FCSTD DOCUMENT  (FreeCAD 0.21R33771 (Git))
Label: YawBearing_Assembly
License: All rights reserved
LicenseURL: http://en.wikipedia.org/wiki/All_rights_reserved
objects: App::Link×4, App::Part×2, Spreadsheet::Sheet×1
EXTERNAL_REF file=YawBearing_Pipe.FCStd obj=Tube
EXTERNAL_REF file=YawBearing_Plate_Top.FCStd obj=PocketBody
EXTERNAL_REF file=../Master_of_Puppets.FCStd obj=Alternator
EXTERNAL_REF file=../Master_of_Puppets.FCStd obj=HighEndStop
EXTERNAL_REF file=../Master_of_Puppets.FCStd obj=Spreadsheet
EXTERNAL_REF file=../Master_of_Puppets.FCStd obj=YawBearing
EXTERNAL_REF file=YawBearing_ArcWireSupport.FCStd obj=PadBody
EXTERNAL_REF file=YawBearing_SafetyCatch.FCStd obj=Body

FEATURE [App::Link] Link  label="Pipe"
  LinkTransform = true
  LinkedObject = -> <external YawBearing_Pipe.FCStd>#Tube
FEATURE [App::Link] Link001  label="Plate_Top"
  LinkPlacement = pos=(-3.525,0,5.995) rot=(1,0,0;-1.5708rad)
  LinkedObject = -> <external YawBearing_Plate_Top.FCStd>#PocketBody
  Placement = pos=(-3.525,0,5.995) rot=(1,0,0;-1.5708rad)
  expr: .Placement.Base.x = Spreadsheet.TopPlateX
  expr: .Placement.Base.z = Spreadsheet.TopPlateZ
FEATURE [Spreadsheet::Sheet] Spreadsheet
  cells = A1='Inputs; A2='YawPipeDiameter; B2(YawPipeDiameter)==Master_of_Puppets#Spreadsheet.YawPipeDiameter; A3='FlatMetalThickness; B3(FlatMetalThickness)==Master_of_Puppets#Spreadsheet.FlatMetalThickness; A4='I; B4(I)==Master_of_Puppets#Alternator.I; A5='k; B5(k)==Master_of_Puppets#Alternator.k; A6='YawBearingPlateTopHoleRadius; B6(YawBearingPlateTopHoleRadius)==Master_of_Puppets#YawBearing.YawBearingPlateTopHoleRadius; A7='SafetyCatchZ; B7(SafetyCatchZ)==Master_of_Puppets#HighEndStop.SafetyCatchZ; A8='SafetyCatchPartAngle; B8(SafetyCatchPartAngle)==Master_of_Puppets#HighEndStop.SafetyCatchAngle; A9='YawPipeLength; B9(YawPipeLength)==Master_of_Puppets#HighEndStop.YawPipeLength; A10='ArcWireSupportLength; B10(ArcWireSupportLength)==Master_of_Puppets#YawBearing.ArcWireSupportLength; A11='Calculated; A12='TopPlateX; B12(TopPlateX)==-I / 2; A13='TopPlateZ; B13(TopPlateZ)==k / 2; A14='ArcWireSupportX; B14(ArcWireSupportX)==-ArcWireSupportLength / 2 - YawBearingPlateTopHoleRadius; A15='ArcWireSupportY; B15(ArcWireSupportY)==FlatMetalThickness; A16='SafetyCatchLinkY; B16(SafetyCatchLinkY)==(YawPipeLength - SafetyCatchZ) * -1; A17='SafetyCatchRotation; B17(SafetyCatchRotation)==create(<<rotation>>; 0; -90; 90); A18='SafetyCatchAxis; B18(SafetyCatchAxis)==.SafetyCatchRotation.Axis; A19='SafetyCatchAngle; B19(SafetyCatchAngle)==.SafetyCatchRotation.Angle * 180 / pi
FEATURE [App::Link] Link002  label="ArcWireSupport"
  LinkPlacement = pos=(-20.6,5,0) rot=(0,0,1;0rad)
  LinkedObject = -> <external YawBearing_ArcWireSupport.FCStd>#PadBody
  Placement = pos=(-20.6,5,0) rot=(0,0,1;0rad)
  expr: .Placement.Base.x = -Spreadsheet.ArcWireSupportLength / 2 - Spreadsheet.YawBearingPlateTopHoleRadius
  expr: .Placement.Base.y = Spreadsheet.ArcWireSupportY
FEATURE [App::Link] Link003  label="SafetyCatch"
  LinkPlacement = pos=(0,-22.4398,0) rot=(0.57735,-0.57735,0.57735;2.0944rad)
  LinkedObject = -> <external YawBearing_SafetyCatch.FCStd>#Body
  Placement = pos=(0,-22.4398,0) rot=(0.57735,-0.57735,0.57735;2.0944rad)
  expr: .LinkPlacement.Base.y = Spreadsheet.SafetyCatchLinkY
  expr: .Placement.Rotation.Angle = Spreadsheet.SafetyCatchAngle
  expr: .Placement.Rotation.Axis = Spreadsheet.SafetyCatchAxis
FEATURE [App::Part] Part001  label="SafetyCatchPart"
  Group = -> [Link003]
  Origin = -> Origin001
  Placement = pos=(0,0,0) rot=(0,-1,0;0.066334rad)
  expr: .Placement.Rotation.Angle = Spreadsheet.SafetyCatchPartAngle
FEATURE [App::Part] Part  label="YawBearing_Assembly"
  Group = -> [Link,Link001,Link002,Part001]
  Origin = -> Origin

RESOLVED EXTERNAL PARTS (link-assembly join: the EXTERNAL_REF files above that resolve inside this repo's crawl, each included once):
---- part ../Master_of_Puppets.FCStd = doc fcstd_6404554055c4 (61625 chars; too large to inline — full recipe in that document) ----
---- part YawBearing_ArcWireSupport.FCStd = doc fcstd_3435764e4c97 ----
FCSTD DOCUMENT  (FreeCAD 0.20R29177 (Git))
Label: YawBearing_ArcWireSupport
License: All rights reserved
LicenseURL: http://en.wikipedia.org/wiki/All_rights_reserved
objects: Sketcher::SketchObject×1, PartDesign::Pad×1, PartDesign::Body×1, Spreadsheet::Sheet×1
note: 4 computed .brp shape members not serialized (recipe doc carries the construction recipe); baked Part::Feature solids carry a one-line shape summary decoded from their .brp
EXTERNAL_REF file=../Master_of_Puppets.FCStd obj=YawBearing

FEATURE [Sketcher::SketchObject] Sketch
  FullyConstrained = true
  MapMode = 5
  Support = -> [XY_Plane001]
  expr: Constraints[8] = Spreadsheet.ArcWireSupportThickness
  expr: Constraints[9] = Spreadsheet.ArcWireSupportLength / 2
  sketch-geometry (4):
    g0: ArcOfCircle CenterX=0 CenterY=0 CenterZ=0 NormalX=0 NormalY=0 NormalZ=1 AngleXU=0 Radius=17.075 StartAngle=-9e-16 EndAngle=3.14159
    g1: ArcOfCircle CenterX=-1e-16 CenterY=0 CenterZ=0 NormalX=0 NormalY=0 NormalZ=1 AngleXU=0 Radius=22.075 StartAngle=-8.9e-15 EndAngle=3.14159
    g2: LineSegment StartX=-22.075 StartY=6.9728e-12 StartZ=0 EndX=-17.075 EndY=-1.268e-13 EndZ=0
    g3: LineSegment StartX=17.075 StartY=-1.52e-14 StartZ=0 EndX=22.075 EndY=-1.961e-13 EndZ=0
  constraints (12):
    c: Coincident(g0,g-1)
    c: PointOnObject(g0,g-1)
    c: PointOnObject(g0,g-1)
    c: Coincident(g1,g-1)
    c: PointOnObject(g1,g-1)
    c: Coincident(g2,g1)
    c: Coincident(g2,g0)
    c: Coincident(g3,g1)
    c: DistanceX(g2,g2) = 5
    c: DistanceX(g-2,g1) = 22.075
    c: Coincident(g0,g3)
    c: PointOnObject(g1,g-1)
FEATURE [PartDesign::Pad] Pad
  AllowMultiFace = false
  Direction = (0,0,1)
  Length = 10
  Length2 = 100
  Midplane = true
  Profile = -> Sketch
  Type = 0
  expr: Length = Spreadsheet.ArcWireSupportWidth
FEATURE [PartDesign::Body] PadBody  label="ArcWireSupport"
  Group = -> [Sketch,Pad]
  Origin = -> Origin001
  Tip = -> Pad
FEATURE [Spreadsheet::Sheet] Spreadsheet
  cells = A1=Inputs; A2=ArcWireSupportThickness; B2(ArcWireSupportThickness)==Master_of_Puppets#YawBearing.ArcWireSupportThickness; A3=ArcWireSupportWidth; B3(ArcWireSupportWidth)==Master_of_Puppets#YawBearing.ArcWireSupportWidth; A4=ArcWireSupportLength; B4(ArcWireSupportLength)==Master_of_Puppets#YawBearing.ArcWireSupportLength
---- part YawBearing_Plate_Top.FCStd = doc fcstd_9ede75f66de1 ----
FCSTD DOCUMENT  (FreeCAD 0.20R29177 (Git))
Label: YawBearing_Plate_Top
License: All rights reserved
LicenseURL: http://en.wikipedia.org/wiki/All_rights_reserved
objects: Sketcher::SketchObject×2, PartDesign::Pad×1, PartDesign::Pocket×1, PartDesign::Body×1, Spreadsheet::Sheet×1
note: 7 computed .brp shape members not serialized (recipe doc carries the construction recipe); baked Part::Feature solids carry a one-line shape summary decoded from their .brp
EXTERNAL_REF file=../Master_of_Puppets.FCStd obj=Alternator
EXTERNAL_REF file=../Master_of_Puppets.FCStd obj=Spreadsheet
EXTERNAL_REF file=../Master_of_Puppets.FCStd obj=YawBearing

FEATURE [Sketcher::SketchObject] Sketch
  FullyConstrained = true
  MapMode = 5
  Support = -> [XY_Plane001]
  expr: Constraints[14] = Spreadsheet.Width
  expr: Constraints[15] = Spreadsheet.Length
  sketch-geometry (6):
    g0: LineSegment StartX=-42.15 StartY=-42.65 StartZ=0 EndX=42.15 EndY=-42.65 EndZ=0
    g1: LineSegment StartX=42.15 StartY=-42.65 StartZ=0 EndX=42.15 EndY=42.65 EndZ=0
    g2: LineSegment StartX=42.15 StartY=42.65 StartZ=0 EndX=-42.15 EndY=42.65 EndZ=0
    g3: LineSegment StartX=-42.15 StartY=42.65 StartZ=0 EndX=-42.15 EndY=-42.65 EndZ=0
    g4: LineSegment StartX=-42.15 StartY=42.65 StartZ=0 EndX=42.15 EndY=-42.65 EndZ=0
    g5: LineSegment StartX=42.15 StartY=42.65 StartZ=0 EndX=-42.15 EndY=-42.65 EndZ=0
  constraints (16):
    c: Coincident(g0,g1)
    c: Coincident(g1,g2)
    c: Coincident(g2,g3)
    c: Coincident(g3,g0)
    c: Horizontal(g0)
    c: Horizontal(g2)
    c: Vertical(g1)
    c: Vertical(g3)
    c: Coincident(g4,g2)
    c: Coincident(g4,g0)
    c: Coincident(g5,g1)
    c: Coincident(g5,g0)
    c: PointOnObject(g-1,g4)
    c: PointOnObject(g-1,g5)
    c: DistanceX(g0,g0) = 84.3
    c: DistanceY(g1,g1) = 85.3
FEATURE [PartDesign::Pad] Pad
  AllowMultiFace = false
  Direction = (0,0,1)
  Length = 10
  Length2 = 100
  Profile = -> Sketch
  Type = 0
  expr: Length = Spreadsheet.FlatMetalThickness
FEATURE [Sketcher::SketchObject] Sketch001
  ExternalGeometry = -> [Pad]
  FullyConstrained = true
  MapMode = 5
  Placement = pos=(0,0,10) rot=(0,0,1;0rad)
  Support = -> [Pad]
  expr: Constraints[12] = Spreadsheet.Hole_x
  expr: Constraints[13] = Spreadsheet.Hole_y
  expr: Constraints[15] = Spreadsheet.YawBearingPlateTopHoleRadius
  expr: Constraints[17] = Spreadsheet.YawPipeRadius
  expr: Constraints[18] = Spreadsheet.YawPipeRadius
  expr: Constraints[19] = Spreadsheet.YawPipeRadius
  expr: Constraints[23] = Spreadsheet.Width
  expr: Constraints[25] = Spreadsheet.YawBearingPlateCornerChamferLength
  sketch-geometry (9):
    g0: LineSegment StartX=-42.15 StartY=-32.65 StartZ=0 EndX=-42.15 EndY=-42.65 EndZ=0
    g1: LineSegment StartX=-42.15 StartY=-42.65 StartZ=0 EndX=-32.15 EndY=-42.65 EndZ=0
    g2: LineSegment StartX=-32.15 StartY=-42.65 StartZ=0 EndX=-42.15 EndY=-32.65 EndZ=0
    g3: LineSegment StartX=-42.15 StartY=12.5 StartZ=0 EndX=12 EndY=12.5 EndZ=0
    g4: LineSegment StartX=12 StartY=12.5 StartZ=0 EndX=12 EndY=-42.65 EndZ=0
    g5: Circle CenterX=12 CenterY=12.5 CenterZ=0 NormalX=0 NormalY=0 NormalZ=1 AngleXU=0 Radius=10
    g6: ArcOfCircle CenterX=12 CenterY=12.5 CenterZ=0 NormalX=0 NormalY=0 NormalZ=1 AngleXU=0 Radius=30.15 StartAngle=1.32574e-06 EndAngle=1.57079
    g7: LineSegment StartX=12.0001 StartY=42.65 StartZ=0 EndX=42.15 EndY=84.3 EndZ=0
    g8: LineSegment StartX=42.15 StartY=84.3 StartZ=0 EndX=42.15 EndY=12.5 EndZ=0
  constraints (26):
    c: PointOnObject(g0,g-3)
    c: Coincident(g0,g-4)
    c: Coincident(g0,g1)
    c: PointOnObject(g1,g-4)
    c: Coincident(g1,g2)
    c: Coincident(g2,g0)
    c: Equal(g0,g1)
    c: PointOnObject(g3,g-3)
    c: Horizontal(g3)
    c: Coincident(g3,g4)
    c: PointOnObject(g4,g-4)
    c: Vertical(g4)
    c: Distance(g3) = 54.15
    c: Distance(g4) = 55.15
    c: Coincident(g5,g3)
    c: Radius(g5) = 10
    c: Coincident(g6,g3)
    c: Radius(g6) = 30.15
    c: DistanceY(g3,g6) = 30.15
    c: DistanceX(g3,g6) = 30.15
    c: Coincident(g6,g7)
    c: Coincident(g8,g6)
    c: Vertical(g8)
    c: DistanceY(g-1,g7) = 84.3
    c: Coincident(g7,g8)
    c: Distance(g1) = 10
FEATURE [PartDesign::Pocket] Pocket
  AllowMultiFace = false
  BaseFeature = -> Pad
  Direction = (0,0,-1)
  Length = 5
  Length2 = 100
  Profile = -> Sketch001
  Type = 1
FEATURE [PartDesign::Body] PocketBody  label="YawBearing_Plate_Top"
  Group = -> [Sketch,Pad,Sketch001,Pocket]
  Openafpm_Flat = true
  Origin = -> Origin001
  Tip = -> Pocket
FEATURE [Spreadsheet::Sheet] Spreadsheet
  cells = A1=Inputs; A2=YawPipeDiameter; B2(YawPipeDiameter)==Master_of_Puppets#Spreadsheet.YawPipeDiameter; A3=RotorDiskRadius; B3(RotorDiskRadius)==Master_of_Puppets#Spreadsheet.RotorDiskRadius; A4=FlatMetalThickness; B4(FlatMetalThickness)==Master_of_Puppets#Spreadsheet.FlatMetalThickness; A5=I; B5(I)==Master_of_Puppets#Alternator.I; A6=k; B6(k)==Master_of_Puppets#Alternator.k; A7=YawBearingPlateTopHoleRadius; B7(YawBearingPlateTopHoleRadius)==Master_of_Puppets#YawBearing.YawBearingPlateTopHoleRadius; A8=YawBearingPlateCornerChamferLength; B8(YawBearingPlateCornerChamferLength)==Master_of_Puppets#YawBearing.YawBearingPlateCornerChamferLength; A9=Calculated; A10=YawPipeRadius; B10(YawPipeRadius)==YawPipeDiameter / 2; A11=Hole_x; B11(Hole_x)==YawPipeRadius + I; A12=Hole_y; B12(Hole_y)==YawPipeRadius + k; A13=Width; B13(Width)==Hole_x + YawPipeRadius; A14=Length; B14(Length)==Hole_y + YawPipeRadius
---- part YawBearing_SafetyCatch.FCStd = doc fcstd_353e2f168a8f ----
FCSTD DOCUMENT  (FreeCAD 0.21R33675 (Git))
Label: YawBearing_SafetyCatch
License: All rights reserved
LicenseURL: http://en.wikipedia.org/wiki/All_rights_reserved
objects: Sketcher::SketchObject×1, PartDesign::Pad×1, PartDesign::Body×1, Spreadsheet::Sheet×1
note: 4 computed .brp shape members not serialized (recipe doc carries the construction recipe); baked Part::Feature solids carry a one-line shape summary decoded from their .brp
EXTERNAL_REF file=../Master_of_Puppets.FCStd obj=HighEndStop
EXTERNAL_REF file=../Master_of_Puppets.FCStd obj=Spreadsheet

FEATURE [Sketcher::SketchObject] Sketch
  FullyConstrained = true
  MapMode = 5
  Placement = pos=(0,0,0) rot=(0,1,0;3.14159rad)
  Support = -> [XY_Plane]
  expr: Constraints[14] = Spreadsheet.Width
  expr: Constraints[15] = Spreadsheet.Length
  expr: Constraints[1] = Spreadsheet.YawPipeRadius
  sketch-geometry (6):
    g0: LineSegment StartX=156.662 StartY=47.7203 StartZ=0 EndX=156.662 EndY=-47.7203 EndZ=0
    g1: LineSegment StartX=57.15 StartY=-47.7203 StartZ=0 EndX=57.15 EndY=47.7202 EndZ=0
    g2: Circle CenterX=0 CenterY=0 CenterZ=0 NormalX=0 NormalY=0 NormalZ=1 AngleXU=0 Radius=57.15
    g3: LineSegment StartX=156.662 StartY=47.7203 StartZ=0 EndX=31.4468 EndY=47.7203 EndZ=0
    g4: LineSegment StartX=156.662 StartY=-47.7203 StartZ=0 EndX=31.4468 EndY=-47.7203 EndZ=0
    g5: ArcOfCircle CenterX=0 CenterY=0 CenterZ=0 NormalX=0 NormalY=0 NormalZ=1 AngleXU=0 Radius=57.15 StartAngle=5.29505 EndAngle=7.27132
  constraints (17):
    c: Symmetric(g0,g0,g-1)
    c: Radius(g2) = 57.15
    c: Tangent(g2,g1)
    c: PointOnObject(g3,g2)
    c: Horizontal(g3)
    c: Coincident(g5,g2)
    c: Coincident(g5,g3)
    c: Coincident(g5,g4)
    c: Horizontal(g4)
    c: Coincident(g4,g0)
    c: Coincident(g3,g0)
    c: Vertical(g1)
    c: PointOnObject(g1,g3)
    c: PointOnObject(g1,g4)
    c: DistanceY(g0,g0) = 95.4405
    c: DistanceX(g1,g0) = 99.5122
    c: Coincident(g5,g-1)
FEATURE [PartDesign::Pad] Pad
  Direction = (0,0,-1)
  Length = 12
  Length2 = 100
  Profile = -> Sketch
  Type = 0
  expr: Length = Spreadsheet.FlatMetalThickness
FEATURE [PartDesign::Body] Body  label="YawBearing_SafetyCatch"
  Group = -> [Sketch,Pad]
  Openafpm_Flat = true
  Origin = -> Origin
  Tip = -> Pad
FEATURE [Spreadsheet::Sheet] Spreadsheet
  cells = A1='Inputs; A2='FlatMetalThickness; B2(FlatMetalThickness)==Master_of_Puppets#Spreadsheet.FlatMetalThickness; A3='YawPipeDiameter; B3(YawPipeDiameter)==Master_of_Puppets#Spreadsheet.YawPipeDiameter; A4='CalculatedWindTurbineShape; B4(CalculatedWindTurbineShape)==Master_of_Puppets#Spreadsheet.CalculatedWindTurbineShape; A5='Width; B5(Width)==Master_of_Puppets#HighEndStop.SafetyCatchWidth; A6='Length; B6(Length)==Master_of_Puppets#HighEndStop.SafetyCatchLength; A7='Calculated; A8='YawPipeRadius; B8(YawPipeRadius)==YawPipeDiameter / 2; A9='DistanceFromOrigin; B9(DistanceFromOrigin)==CalculatedWindTurbineShape == <<T>> ? 0 : YawPipeRadius
